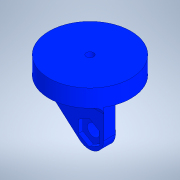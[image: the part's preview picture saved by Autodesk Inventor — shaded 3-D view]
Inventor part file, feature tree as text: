
AUTODESK INVENTOR PART (.ipt)
format: ipt  version: 2020 (Build 240168000, 168)  size: 205,312 bytes
history: native  units: mm
features: extrude x6, sketch x6, chamfer x3, projected_geometry x1
ambient origin geometry x8: Origin, YZ Plane, XZ Plane, XY Plane, X Axis, Y Axis, Z Axis, Center Point
bodies: Solid1 (feature_tree)
feature tree (16):
  extrude  "Extrusion1"  Depth=10.0mm
  extrude  "Extrusion2"  TaperAngle=0.0deg  [1 undecoded]
  extrude  "Extrusion3"  Depth=7.4mm
  chamfer  "Chamfer1"  Distance=1.5mm
  extrude  "Extrusion6"  Depth=0.8mm TaperAngle=0.0deg
  extrude  "Extrusion7"  Depth=2.0mm
  chamfer  "Chamfer2"  Distance=2.5mm
  extrude  "Extrusion8"  Depth=2.5mm
  chamfer  "Chamfer3"  Distance=3.0mm
  sketch  "Sketch1"  dims[d0=10.0mm d1=4.2mm]
  sketch  "Sketch2"  dims[d2=12.5mm d4=0.0mm]
  sketch  "Sketch4"  dims[d5=3.0mm d6=0.0mm d7=7.4mm d8=1.5mm d9=0.0mm]
  sketch  "Sketch6"  dims[d10=8.5mm d11=0.8mm d12=0.0mm]
  projected_geometry  "Projected Loop1"
  sketch  "Sketch7"  dims[d13=0.8mm d14=2.0mm d15=45.0deg d25=14.0mm]
  sketch  "Sketch8"  dims[d26=6.0mm d27=2.5mm d28=2.5mm d29=3.0mm d30=0.0mm d31=7.0mm d32=6.0mm d33=0.0mm d34=2.0mm d35=2.0mm d36=45.0deg d37=2.0mm d38=0.0mm d39=2.0mm d40=2.0mm d41=45.0deg]
note: 1 required parameter value undecoded (feature->parameter linkage not recoverable at this tier; creation-order binding heuristic only, values carry confidence <= 0.55)
